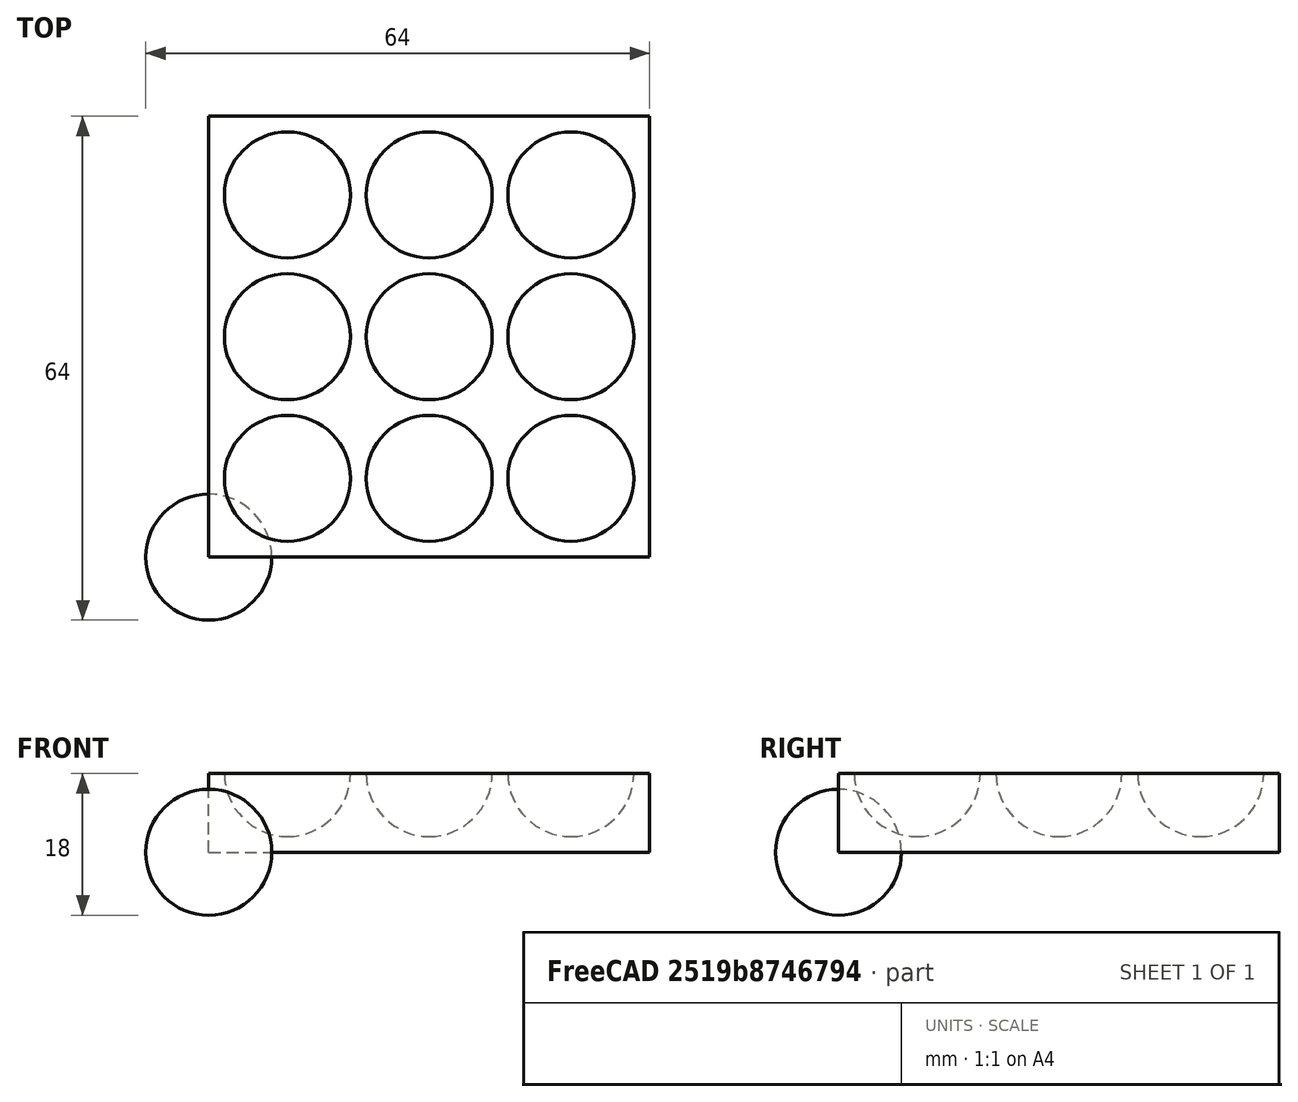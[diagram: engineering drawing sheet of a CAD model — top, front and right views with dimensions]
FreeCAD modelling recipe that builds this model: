
FCSTD DOCUMENT  (FreeCAD 0.21R33694 (Git))
Label: OJT1_T013P012_porta_caniques
License: All rights reserved
LicenseURL: http://en.wikipedia.org/wiki/All_rights_reserved
objects: Part::Sphere×1, Part::FeaturePython×1, Part::Box×1, Part::Cut×1
note: 3 computed .brp shape members not serialized (recipe doc carries the construction recipe); baked Part::Feature solids carry a one-line shape summary decoded from their .brp

FEATURE [Part::Sphere] Sphere
  Angle1 = -90
  Angle2 = 90
  Angle3 = 360
  AttacherType = Attacher::AttachEngine3D
  Radius = 8
FEATURE [Part::FeaturePython] Array  # Draft array (typed FeaturePython)
  AlwaysSyncPlacement = false
  Angle = 360
  ArrayType = 0
  Axis = (0,0,1)
  Base = -> Sphere
  Center = (0,0,0)
  Count = 9
  ExpandArray = false
  Fuse = false
  IntervalAxis = (0,0,0)
  IntervalX = (18,0,0)
  IntervalY = (0,18,0)
  IntervalZ = (0,0,100)
  NumberCircles = 3
  NumberPolar = 5
  NumberX = 3
  NumberY = 3
  NumberZ = 1
  Placement = pos=(10,10,10) rot=(0,0,1;0rad)
  PlacementList = 9 placements: [(0,0,0),(0,18,0),(0,36,0),(18,0,0),(18,18,0),(18,36,0),(36,0,0),(36,18,0),(36,36,0)]
  RadialDistance = 50
  ScaleList = (9) [(1,1,1),(1,1,1),(1,1,1),(1,1,1),(1,1,1),(1,1,1),(1,1,1),(1,1,1),(1,1,1)]
  Symmetry = 1
  TangentialDistance = 25
FEATURE [Part::Box] Box  label="Cube"
  AttacherType = Attacher::AttachEngine3D
  Height = 10
  Length = 56
  Width = 56
FEATURE [Part::Cut] Cut
  Base = -> Box
  Refine = true
  Tool = -> Array
